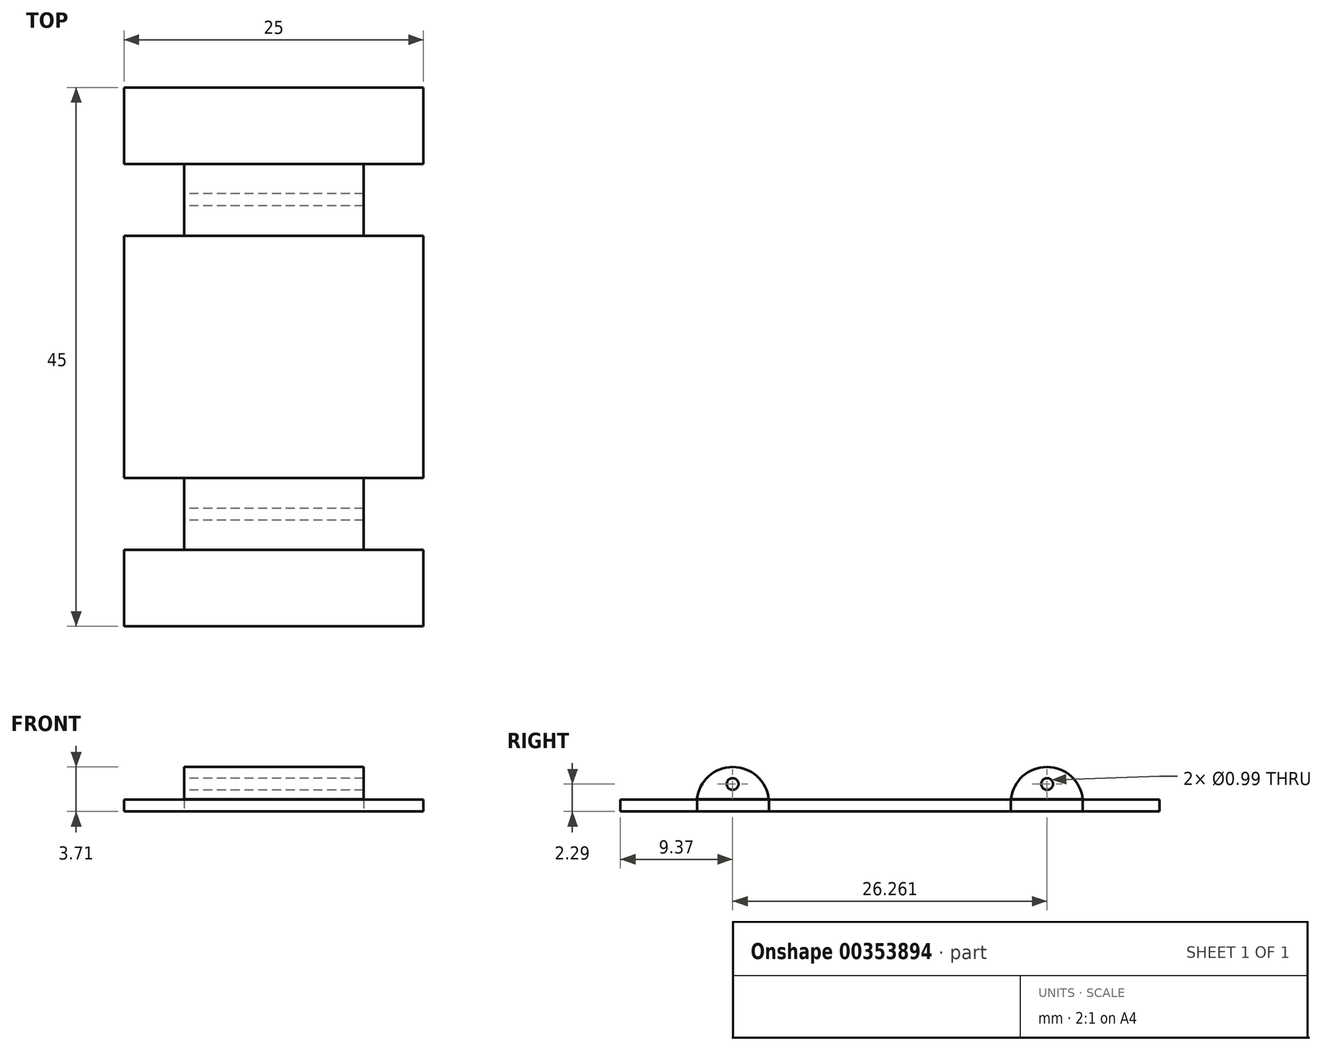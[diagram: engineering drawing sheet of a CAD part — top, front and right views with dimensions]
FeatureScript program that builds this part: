
annotation { "Feature Type Name" : "Feature", "Feature Type Description" : "" }
export const myFeature = defineFeature(function(context is Context, id is Id, definition is map)
    precondition{}
    {
        {
            var Q0;
            Q0=qCreatedBy(makeId("Top.planeOp"),FACE);
            var sketch = newSketch(context, id + "F0", { "sketchPlane" : qUnion([Q0])});
            skLineSegment(sketch, "E0.bottom", {"start": v(12.5, 22.5) * mm, "end": v(-12.5, 22.5) * mm});
            skLineSegment(sketch, "E0.top", {"start": v(12.5, -22.5) * mm, "end": v(-12.5, -22.5) * mm});
            skLineSegment(sketch, "E0.left", {"start": v(12.5, 22.5) * mm, "end": v(12.5, 16.1) * mm});
            skLineSegment(sketch, "E0.right", {"start": v(-12.5, 22.5) * mm, "end": v(-12.5, 16.1) * mm});
            skPoint(sketch, "E0.middle", {"position": v(0, 0) * mm});
            skLineSegment(sketch, "E1.bottom", {"start": v(-12.5, 16.1) * mm, "end": v(-7.5, 16.1) * mm});
            skLineSegment(sketch, "E1.top", {"start": v(-12.5, 10.1) * mm, "end": v(-7.5, 10.1) * mm});
            skLineSegment(sketch, "E1.right", {"start": v(-7.5, 16.1) * mm, "end": v(-7.5, 10.1) * mm});
            skLineSegment(sketch, "E2.MirrorCS", {"start": v(12.5, 16.1) * mm, "end": v(7.5, 16.1) * mm});
            skLineSegment(sketch, "E3.MirrorCS", {"start": v(7.5, 16.1) * mm, "end": v(7.5, 10.1) * mm});
            skLineSegment(sketch, "E4.MirrorCS", {"start": v(12.5, 10.1) * mm, "end": v(7.5, 10.1) * mm});
            skLineSegment(sketch, "E5.MirrorCS", {"start": v(12.5, -10.1) * mm, "end": v(7.5, -10.1) * mm});
            skLineSegment(sketch, "E6.MirrorCS", {"start": v(7.5, -16.1) * mm, "end": v(7.5, -10.1) * mm});
            skLineSegment(sketch, "E7.MirrorCS", {"start": v(12.5, -16.1) * mm, "end": v(7.5, -16.1) * mm});
            skLineSegment(sketch, "E8.MirrorCS", {"start": v(-12.5, -10.1) * mm, "end": v(-7.5, -10.1) * mm});
            skLineSegment(sketch, "E9.MirrorCS", {"start": v(-7.5, -16.1) * mm, "end": v(-7.5, -10.1) * mm});
            skLineSegment(sketch, "E10.MirrorCS", {"start": v(-12.5, -16.1) * mm, "end": v(-7.5, -16.1) * mm});
            skLineSegment(sketch, "E11.trimOffspring", {"start": v(12.5, 10.1) * mm, "end": v(12.5, -10.1) * mm});
            skLineSegment(sketch, "E12.trimOffspring", {"start": v(12.5, -16.1) * mm, "end": v(12.5, -22.5) * mm});
            skLineSegment(sketch, "E13.trimOffspring", {"start": v(-12.5, -16.1) * mm, "end": v(-12.5, -22.5) * mm});
            skLineSegment(sketch, "E14.trimOffspring", {"start": v(-12.5, 10.1) * mm, "end": v(-12.5, -10.1) * mm});
            skSolve(sketch);
        }
        {
            var Q0;
            Q0 = qSketchRegion(id + "F0", true);
            extrude(context, id + "F1", {"entities" : qUnion([Q0]), "endBound" : BoundingType.SYMMETRIC, "depth" : 1 * mm});
        }
        {
            var Q0;
            Q0=qCreatedBy(makeId("Right.planeOp"),FACE);
            var sketch = newSketch(context, id + "F2", { "sketchPlane" : qUnion([Q0])});
            skArc(sketch, "E15", {"start": v(16.11, 0.5) * mm, "mid": v(13.12, 3.21) * mm, "end": v(10.11, 0.52) * mm});
            skArc(sketch, "E16.MirrorCS", {"start": v(-16.11, 0.5) * mm, "mid": v(-13.12, 3.21) * mm, "end": v(-10.11, 0.52) * mm});
            skCircle(sketch, "E17", {"center": v(13.13, 1.79) * mm, "radius": 0.5 * mm});
            skCircle(sketch, "E18.MirrorC", {"center": v(-13.13, 1.79) * mm, "radius": 0.5 * mm});
            skLineSegment(sketch, "E19", {"start": v(16.11, 0.5) * mm, "end": v(10.11, 0.52) * mm});
            skLineSegment(sketch, "E20", {"start": v(-10.11, 0.52) * mm, "end": v(-16.11, 0.5) * mm});
            skSolve(sketch);
        }
        {
            var Q0;
            Q0 = qSketchRegion(id + "F2", true);
            extrude(context, id + "F3", {"entities" : qUnion([Q0]), "operationType" : NewBodyOperationType.ADD, "endBound" : BoundingType.SYMMETRIC, "depth" : 15 * mm});
        }
    });
